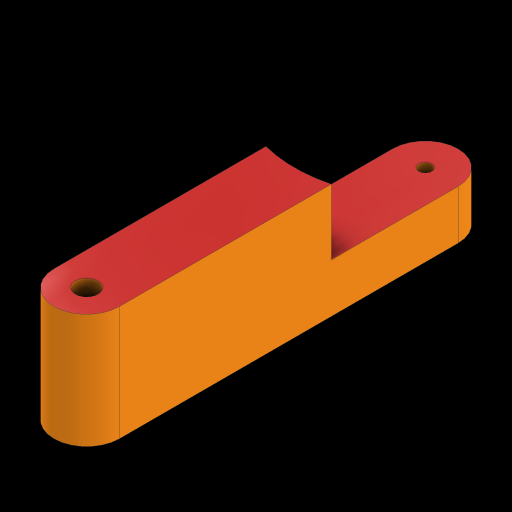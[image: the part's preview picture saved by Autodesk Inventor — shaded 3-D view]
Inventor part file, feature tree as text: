
AUTODESK INVENTOR PART (.ipt)
format: ipt  version: 2023 (Build 270158000, 158)  size: 273,408 bytes
history: native  units: mm
features: extrude x2, sketch x1
ambient origin geometry x8: Origin, YZ Plane, XZ Plane, XY Plane, X Axis, Y Axis, Z Axis, Center Point
bodies: Solid1 (feature_tree)
feature tree (3):
  sketch  "Sketch1"  dims[d1=120.0mm d2=200.0mm d3=15.0deg d4=10.0mm d5=10.0mm d6=80.0mm d7=360.0deg d8=7.0mm d9=4.0mm d10=20.0mm d11=20.0mm d12=20.0mm d13=0.0mm d14=15.0mm d15=0.0mm]
  extrude  "Extrusion1"  Depth=20.0mm
  extrude  "Extrusion2"  Depth=20.0mm
